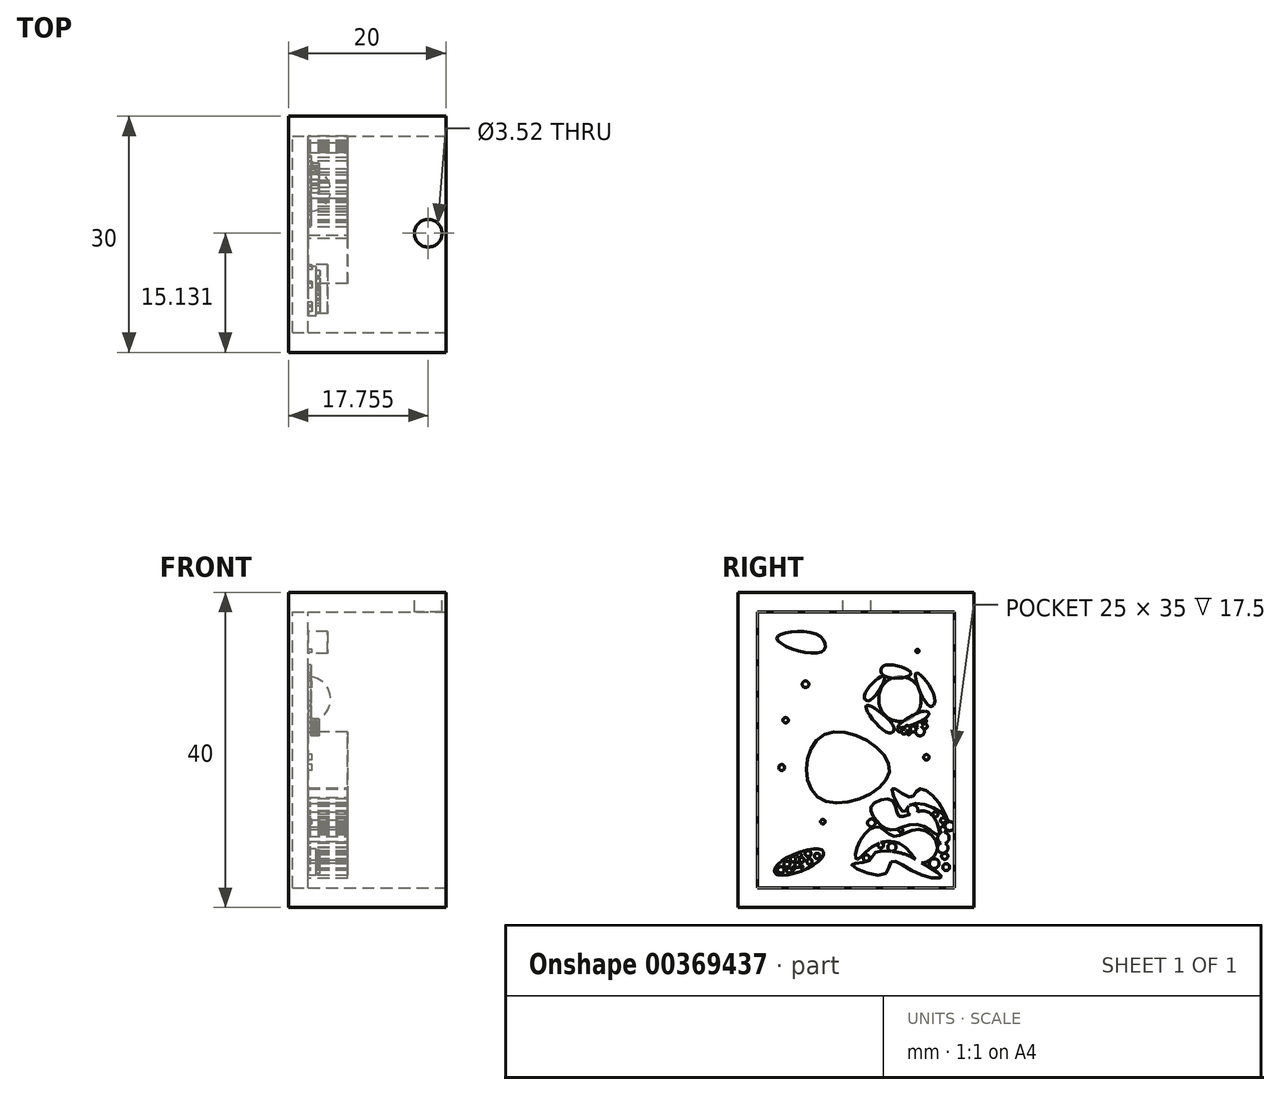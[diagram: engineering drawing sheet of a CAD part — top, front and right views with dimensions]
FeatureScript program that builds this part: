
annotation { "Feature Type Name" : "Feature", "Feature Type Description" : "" }
export const myFeature = defineFeature(function(context is Context, id is Id, definition is map)
    precondition{}
    {
        {
            var Q0;
            Q0=qCreatedBy(makeId("Front.planeOp"),FACE);
            var sketch = newSketch(context, id + "F0", { "sketchPlane" : qUnion([Q0])});
            skLineSegment(sketch, "E0.bottom", {"start": v(0, 0) * mm, "end": v(20, 0) * mm});
            skLineSegment(sketch, "E0.top", {"start": v(0, 40) * mm, "end": v(20, 40) * mm});
            skLineSegment(sketch, "E0.left", {"start": v(0, 0) * mm, "end": v(0, 40) * mm});
            skLineSegment(sketch, "E0.right", {"start": v(20, 0) * mm, "end": v(20, 40) * mm});
            skSolve(sketch);
        }
        {
            var Q0;
            Q0 = qSketchRegion(id + "F0", true);
            extrude(context, id + "F1", {"entities" : qUnion([Q0]), "depth" : 30 * mm});
        }
        {
            var Q0;
            Q0=makeQuery(id+"F1.opExtrude","CAP_FACE",FACE,{"disambiguationData":[OSD([sQuery(id+"F0.wireOp",EDGE,"E0.bottom"),sQuery(id+"F0.wireOp",EDGE,"E0.top"),sQuery(id+"F0.wireOp",EDGE,"E0.left"),sQuery(id+"F0.wireOp",EDGE,"E0.right")])],"isStart":false});
            var sketch = newSketch(context, id + "F2", { "sketchPlane" : qUnion([Q0])});
            skSolve(sketch);
        }
        {
            var Q0;
            Q0=makeQuery(id+"F1.opExtrude","SWEPT_FACE",FACE,{"disambiguationData":[OSD([sQuery(id+"F0.wireOp",EDGE,"E0.right")])]});
            shell(context, id + "F3", {"entities" : qUnion([Q0]), "thickness" : 2.5 * mm});
        }
        {
            var Q0;
            Q0=makeQuery(id+"F3.opShell","OFFSET_FACE",FACE,{"disambiguationData":[OSD([sQuery(id+"F0.wireOp",EDGE,"E0.left")])]});
            var sketch = newSketch(context, id + "F4", { "sketchPlane" : qUnion([Q0])});
            skLineSegment(sketch, "E1", {"start": v(-6.74, 26.46) * mm, "end": v(-12.09, 26.46) * mm});
            skArc(sketch, "E2", {"start": v(-12.09, 26.46) * mm, "mid": v(-9.41, 23.6) * mm, "end": v(-6.74, 26.46) * mm});
            skSolve(sketch);
        }
        {
            var Q0;
            Q0 = qSketchRegion(id + "F4", true);
            var Q1;
            Q1=sQuery(id+"F4.wireOp",EDGE,"E1");
            revolve(context, id + "F5", {"entities" : qUnion([Q0]), "axis" : qUnion([Q1]), "revolveType" : RevolveType.ONE_DIRECTION, "angle" : 180 * degree});
        }
        {
            var Q0;
            Q0=makeQuery(id+"F3.opShell","OFFSET_FACE",FACE,{"disambiguationData":[OSD([sQuery(id+"F0.wireOp",EDGE,"E0.left")])]});
            var sketch = newSketch(context, id + "F6", { "sketchPlane" : qUnion([Q0])});
            skFitSpline(sketch, "E3", {"points": [v(-19.41, 32.44) * mm, v(-25.05, 34.16) * mm, v(-19.76, 34.55) * mm, v(-19.41, 32.44) * mm]});
            skSolve(sketch);
        }
        {
            var Q0;
            Q0 = qSketchRegion(id + "F6", true);
            extrude(context, id + "F7", {"entities" : qUnion([Q0]), "depth" : 2.5 * mm});
        }
        {
            var Q0;
            Q0=makeQuery(id+"F3.opShell","OFFSET_FACE",FACE,{"disambiguationData":[OSD([sQuery(id+"F0.wireOp",EDGE,"E0.left")])]});
            extrude(context, id + "F8", {"entities" : qUnion([Q0]), "oppositeDirection" : true, "depth" : 2 * mm});
        }
        {
            var Q0;
            Q0=makeQuery(id+"F8.opExtrude","CAP_FACE",FACE,{"disambiguationData":[OSD([sQuery(id+"F0.wireOp",EDGE,"E0.left")])],"isStart":true});
            var sketch = newSketch(context, id + "F9", { "sketchPlane" : qUnion([Q0])});
            skFitSpline(sketch, "E4", {"points": [v(-19.02, 21.95) * mm, v(-10.73, 17.37) * mm, v(-19.65, 13.84) * mm, v(-19.02, 21.95) * mm]});
            skSolve(sketch);
        }
        {
            var Q0;
            Q0 = qSketchRegion(id + "F9", true);
            extrude(context, id + "F10", {"entities" : qUnion([Q0]), "depth" : 5 * mm});
        }
        {
            var Q0;
            Q0=makeQuery(id+"F8.opExtrude","CAP_FACE",FACE,{"disambiguationData":[OSD([sQuery(id+"F0.wireOp",EDGE,"E0.left")])],"isStart":true});
            var sketch = newSketch(context, id + "F11", { "sketchPlane" : qUnion([Q0])});
            skEllipse(sketch, "E5", {"center": v(-22.23, 5.74) * mm, "majorRadius": 3.37 * mm, "minorRadius": 1.17 * mm, "majorAxis": v(0.92, 0.38)});
            skSolve(sketch);
        }
        {
            var Q0;
            Q0 = qSketchRegion(id + "F11", true);
            extrude(context, id + "F12", {"entities" : qUnion([Q0]), "depth" : 1 * mm});
        }
        {
            var Q0;
            Q0=makeQuery(id+"F12.opExtrude","CAP_FACE",FACE,{"disambiguationData":[OSD([sQuery(id+"F11.wireOp",EDGE,"E5")])],"isStart":false});
            var sketch = newSketch(context, id + "F13", { "sketchPlane" : qUnion([Q0])});
            skCircle(sketch, "E6", {"center": v(-19.93, 6.53) * mm, "radius": 0.35 * mm});
            skCircle(sketch, "E7", {"center": v(-20.91, 5.81) * mm, "radius": 0.35 * mm});
            skCircle(sketch, "E8", {"center": v(-21.08, 6.83) * mm, "radius": 0.38 * mm});
            skCircle(sketch, "E9", {"center": v(-22.43, 5.38) * mm, "radius": 0.33 * mm});
            skCircle(sketch, "E10", {"center": v(-22.23, 6.6) * mm, "radius": 0.3 * mm});
            skCircle(sketch, "E11", {"center": v(-23.77, 5.5) * mm, "radius": 0.37 * mm});
            skCircle(sketch, "E12", {"center": v(-23.48, 4.67) * mm, "radius": 0.33 * mm});
            skCircle(sketch, "E13", {"center": v(-23.02, 6.12) * mm, "radius": 0.34 * mm});
            skCircle(sketch, "E14", {"center": v(-21.9, 6.01) * mm, "radius": 0.32 * mm});
            skCircle(sketch, "E15", {"center": v(-21.93, 5.14) * mm, "radius": 0.18 * mm});
            skCircle(sketch, "E16", {"center": v(-22.98, 4.92) * mm, "radius": 0.2 * mm});
            skCircle(sketch, "E17", {"center": v(-24.54, 4.75) * mm, "radius": 0.41 * mm});
            skSolve(sketch);
        }
        {
            var Q0;
            Q0 = qSketchRegion(id + "F13", true);
            extrude(context, id + "F14", {"entities" : qUnion([Q0]), "depth" : 0.5 * mm});
        }
        {
            var Q0;
            Q0=makeQuery(id+"F8.opExtrude","CAP_FACE",FACE,{"disambiguationData":[OSD([sQuery(id+"F0.wireOp",EDGE,"E0.left")])],"isStart":true});
            var sketch = newSketch(context, id + "F15", { "sketchPlane" : qUnion([Q0])});
            skFitSpline(sketch, "E18", {"points": [v(-5.66, 25.56) * mm, v(-7.4, 29.71) * mm, v(-5.02, 26.7) * mm, v(-5.66, 25.56) * mm]});
            skFitSpline(sketch, "E19", {"points": [v(-6.32, 24.92) * mm, v(-9.65, 22.87) * mm, v(-5.86, 24.32) * mm, v(-6.32, 24.92) * mm]});
            skFitSpline(sketch, "E20", {"points": [v(-10.2, 22.87) * mm, v(-13.7, 25.61) * mm, v(-11, 22.2) * mm, v(-10.2, 22.87) * mm]});
            skFitSpline(sketch, "E21", {"points": [v(-13.27, 26.3) * mm, v(-11.42, 29.4) * mm, v(-13.91, 26.93) * mm, v(-13.27, 26.3) * mm]});
            skFitSpline(sketch, "E22", {"points": [v(-11.42, 29.4) * mm, v(-8.03, 29.71) * mm, v(-11.42, 30.7) * mm, v(-11.42, 29.4) * mm]});
            skSolve(sketch);
        }
        {
            var Q0;
            Q0 = qSketchRegion(id + "F15", true);
            extrude(context, id + "F16", {"entities" : qUnion([Q0]), "depth" : 0.4 * mm});
        }
        {
            var Q0;
            Q0=makeQuery(id+"F8.opExtrude","CAP_FACE",FACE,{"disambiguationData":[OSD([sQuery(id+"F0.wireOp",EDGE,"E0.left")])],"isStart":true});
            var sketch = newSketch(context, id + "F17", { "sketchPlane" : qUnion([Q0])});
            skFitSpline(sketch, "E23", {"points": [v(-14.64, 8.14) * mm, v(-12.23, 10.2) * mm, v(-10.2, 9.04) * mm, v(-7, 9.9) * mm, v(-4.65, 7.53) * mm, v(-6.7, 5.65) * mm, v(-8.83, 7.7) * mm, v(-12.64, 7.88) * mm, v(-14.92, 6.05) * mm, v(-14.64, 8.14) * mm]});
            skFitSpline(sketch, "E24", {"points": [v(-12.58, 11.27) * mm, v(-10.52, 9.82) * mm, v(-7.04, 10.5) * mm, v(-4.49, 9.25) * mm, v(-5.98, 12.15) * mm, v(-9.48, 11.53) * mm, v(-10.38, 13.54) * mm, v(-13.03, 12.9) * mm, v(-12.58, 11.27) * mm]});
            skFitSpline(sketch, "E25", {"points": [v(-4.46, 12.24) * mm, v(-8.2, 12.93) * mm, v(-9, 12.13) * mm, v(-10.38, 15.11) * mm, v(-8.03, 13.97) * mm, v(-7.08, 14.99) * mm, v(-4.68, 13.54) * mm, v(-3.38, 11.1) * mm, v(-4.46, 12.24) * mm]});
            skFitSpline(sketch, "E26", {"points": [v(-9.08, 6.84) * mm, v(-12.64, 6.93) * mm, v(-13.42, 5.86) * mm, v(-15.52, 5.42) * mm, v(-11.48, 4.17) * mm, v(-10.47, 5.8) * mm, v(-7.08, 4.27) * mm, v(-4.17, 3.88) * mm, v(-6.7, 5.65) * mm, v(-9.08, 6.84) * mm]});
            skCircle(sketch, "E27", {"center": v(-3.93, 11.03) * mm, "radius": 0.34 * mm});
            skCircle(sketch, "E28", {"center": v(-3.97, 9.87) * mm, "radius": 0.39 * mm});
            skCircle(sketch, "E29", {"center": v(-3.11, 10.3) * mm, "radius": 0.58 * mm});
            skCircle(sketch, "E30", {"center": v(-3.9, 8.82) * mm, "radius": 0.73 * mm});
            skCircle(sketch, "E31", {"center": v(-3.99, 7.53) * mm, "radius": 0.67 * mm});
            skCircle(sketch, "E32", {"center": v(-5.06, 5.56) * mm, "radius": 0.61 * mm});
            skCircle(sketch, "E33", {"center": v(-3.54, 5.1) * mm, "radius": 0.44 * mm});
            skCircle(sketch, "E34", {"center": v(-3.73, 6.49) * mm, "radius": 0.4 * mm});
            skCircle(sketch, "E35", {"center": v(-9.33, 9.82) * mm, "radius": 0.26 * mm});
            skCircle(sketch, "E36", {"center": v(-10.43, 7.65) * mm, "radius": 0.53 * mm});
            skCircle(sketch, "E37", {"center": v(-13.68, 6.26) * mm, "radius": 0.4 * mm});
            skCircle(sketch, "E38", {"center": v(-11.86, 7.88) * mm, "radius": 0.35 * mm});
            skCircle(sketch, "E39", {"center": v(-13.03, 10.72) * mm, "radius": 0.5 * mm});
            skCircle(sketch, "E40", {"center": v(-7.82, 12.38) * mm, "radius": 0.67 * mm});
            skCircle(sketch, "E41", {"center": v(-4.92, 11.8) * mm, "radius": 0.33 * mm});
            skSolve(sketch);
        }
        {
            var Q0;
            Q0 = qSketchRegion(id + "F17", true);
            extrude(context, id + "F18", {"entities" : qUnion([Q0]), "depth" : 5 * mm});
        }
        {
            var Q0;
            Q0=makeQuery(id+"F16.opExtrude","CAP_FACE",FACE,{"disambiguationData":[OSD([sQuery(id+"F15.wireOp",EDGE,"E21"),sQuery(id+"F15.wireOp",EDGE,"E22")])],"isStart":false});
            var sketch = newSketch(context, id + "F19", { "sketchPlane" : qUnion([Q0])});
            skCircle(sketch, "E42", {"center": v(-8.9, 22.3) * mm, "radius": 0.3 * mm});
            skCircle(sketch, "E43", {"center": v(-7.75, 22.65) * mm, "radius": 0.37 * mm});
            skCircle(sketch, "E44", {"center": v(-8.3, 22.15) * mm, "radius": 0.22 * mm});
            skCircle(sketch, "E45", {"center": v(-6.9, 23.17) * mm, "radius": 0.38 * mm});
            skCircle(sketch, "E46", {"center": v(-9.48, 22.57) * mm, "radius": 0.28 * mm});
            skCircle(sketch, "E47", {"center": v(-8.48, 22.75) * mm, "radius": 0.34 * mm});
            skCircle(sketch, "E48", {"center": v(-6.87, 22.34) * mm, "radius": 0.56 * mm});
            skCircle(sketch, "E49", {"center": v(-6.27, 23.7) * mm, "radius": 0.23 * mm});
            skCircle(sketch, "E50", {"center": v(-6.27, 23) * mm, "radius": 0.32 * mm});
            skSolve(sketch);
        }
        {
            var Q0;
            Q0 = qSketchRegion(id + "F19", true);
            extrude(context, id + "F20", {"entities" : qUnion([Q0]), "operationType" : NewBodyOperationType.ADD, "depth" : 1 * mm});
        }
        {
            var Q0;
            Q0=makeQuery(id+"F1.opExtrude","SWEPT_FACE",FACE,{"disambiguationData":[OSD([sQuery(id+"F0.wireOp",EDGE,"E0.top")])]});
            var sketch = newSketch(context, id + "F21", { "sketchPlane" : qUnion([Q0])});
            skCircle(sketch, "E51", {"center": v(17.76, -14.87) * mm, "radius": 1.76 * mm});
            skSolve(sketch);
        }
        {
            var Q0;
            Q0 = qSketchRegion(id + "F21", true);
            extrude(context, id + "F22", {"entities" : qUnion([Q0]), "operationType" : NewBodyOperationType.REMOVE, "oppositeDirection" : true, "depth" : 25 * mm});
        }
        {
            var Q0;
            Q0=makeQuery(id+"F8.opExtrude","CAP_FACE",FACE,{"disambiguationData":[OSD([sQuery(id+"F0.wireOp",EDGE,"E0.left")])],"isStart":true});
            var sketch = newSketch(context, id + "F23", { "sketchPlane" : qUnion([Q0])});
            skCircle(sketch, "E52", {"center": v(-21.42, 28.33) * mm, "radius": 0.42 * mm});
            skCircle(sketch, "E53", {"center": v(-23.94, 23.77) * mm, "radius": 0.34 * mm});
            skCircle(sketch, "E54", {"center": v(-6.06, 19.06) * mm, "radius": 0.35 * mm});
            skCircle(sketch, "E55", {"center": v(-19.21, 10.87) * mm, "radius": 0.28 * mm});
            skCircle(sketch, "E56", {"center": v(-24.44, 17.75) * mm, "radius": 0.38 * mm});
            skCircle(sketch, "E57", {"center": v(-7.2, 32.57) * mm, "radius": 0.2 * mm});
            skSolve(sketch);
        }
        {
            var Q0;
            Q0 = qSketchRegion(id + "F23", true);
            extrude(context, id + "F24", {"entities" : qUnion([Q0]), "depth" : 0.5 * mm});
        }
    });
